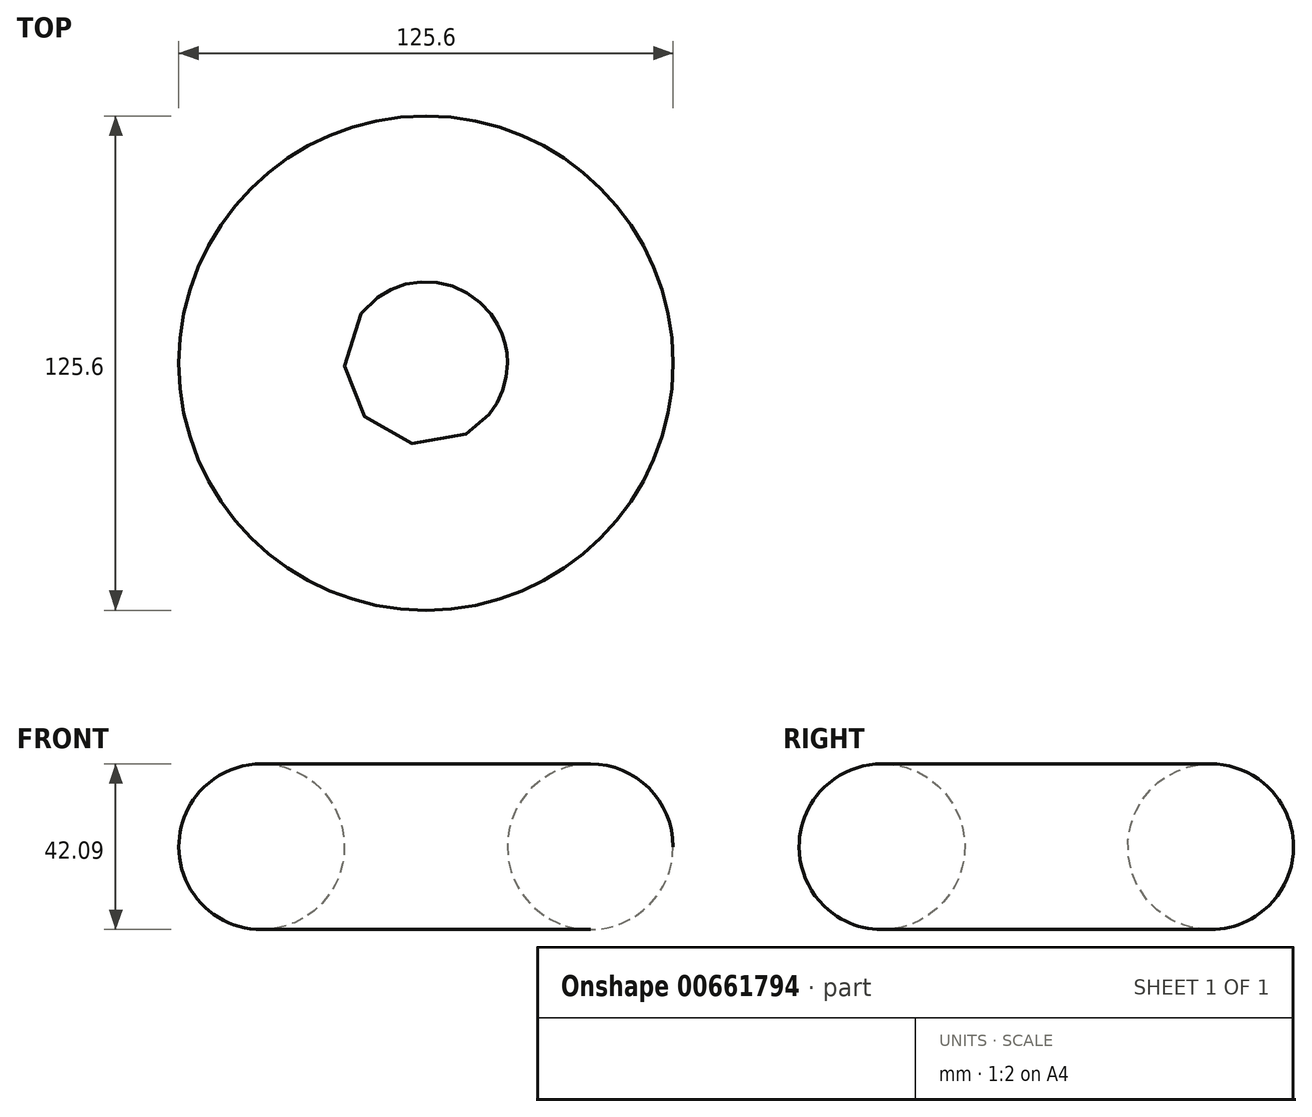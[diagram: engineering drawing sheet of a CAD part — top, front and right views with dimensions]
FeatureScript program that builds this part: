
annotation { "Feature Type Name" : "Feature", "Feature Type Description" : "" }
export const myFeature = defineFeature(function(context is Context, id is Id, definition is map)
    precondition{}
    {
        {
            var Q0;
            Q0=qCreatedBy(makeId("Front.planeOp"),FACE);
            var sketch = newSketch(context, id + "F0", { "sketchPlane" : qUnion([Q0])});
            skCircle(sketch, "E0", {"center": v(-41.75, 47.74) * mm, "radius": 21.05 * mm});
            skLineSegment(sketch, "E1", {"start": v(0, 99.4) * mm, "end": v(0, -95.72) * mm, "construction": true});
            skSolve(sketch);
        }
        {
            var Q0;
            Q0=makeQuery(id+"F0.imprint","IMPRINT",FACE,{"disambiguationData":[TD([[makeQuery(id+"F0.imprint","IMPRINT",EDGE,{"derivedFrom":sQuery(id+"F0.wireOp",EDGE,"E0")}),1.0]])]});
            var Q1;
            Q1=sQuery(id+"F0.wireOp",EDGE,"E1");
            revolve(context, id + "F1", {"entities" : qUnion([Q0]), "axis" : qUnion([Q1]), "revolveType" : RevolveType.FULL});
        }
    });
